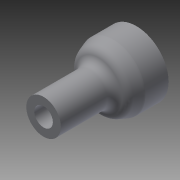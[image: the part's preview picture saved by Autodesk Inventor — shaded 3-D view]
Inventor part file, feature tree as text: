
AUTODESK INVENTOR PART (.ipt)
format: ipt  version: 2015 (Build 190159000, 159)  size: 134,656 bytes
history: native  units: in
note: dims shown in document units (in); Inventor stores cm internally (conversion verified against a paired STEP export)
features: extrude x4, sketch x4, fillet x1
ambient origin geometry x8: Origin, YZ Plane, XZ Plane, XY Plane, X Axis, Y Axis, Z Axis, Center Point
bodies: Solid1 (feature_tree)
feature tree (9):
  extrude  "Extrusion1"  Depth=0.3125in
  extrude  "Extrusion3"  Depth=0.25in
  extrude  "Extrusion4"  Depth=0.125in
  extrude  "Extrusion5"  [1 undecoded]
  fillet  "Fillet1"  [1 undecoded]
  sketch  "Sketch1"  dims[d0=0.3125in d1=0.0in d4=0.1875in d5=-0.1374in]
  sketch  "Sketch3"  dims[d6=0.75in d7=0.0in d8=0.25in]
  sketch  "Sketch4"  dims[d9=0.375in d10=0.0in d11=0.125in]
  sketch  "Sketch5"
note: 2 required parameter values undecoded (feature->parameter linkage not recoverable at this tier; creation-order binding heuristic only, values carry confidence <= 0.55)
